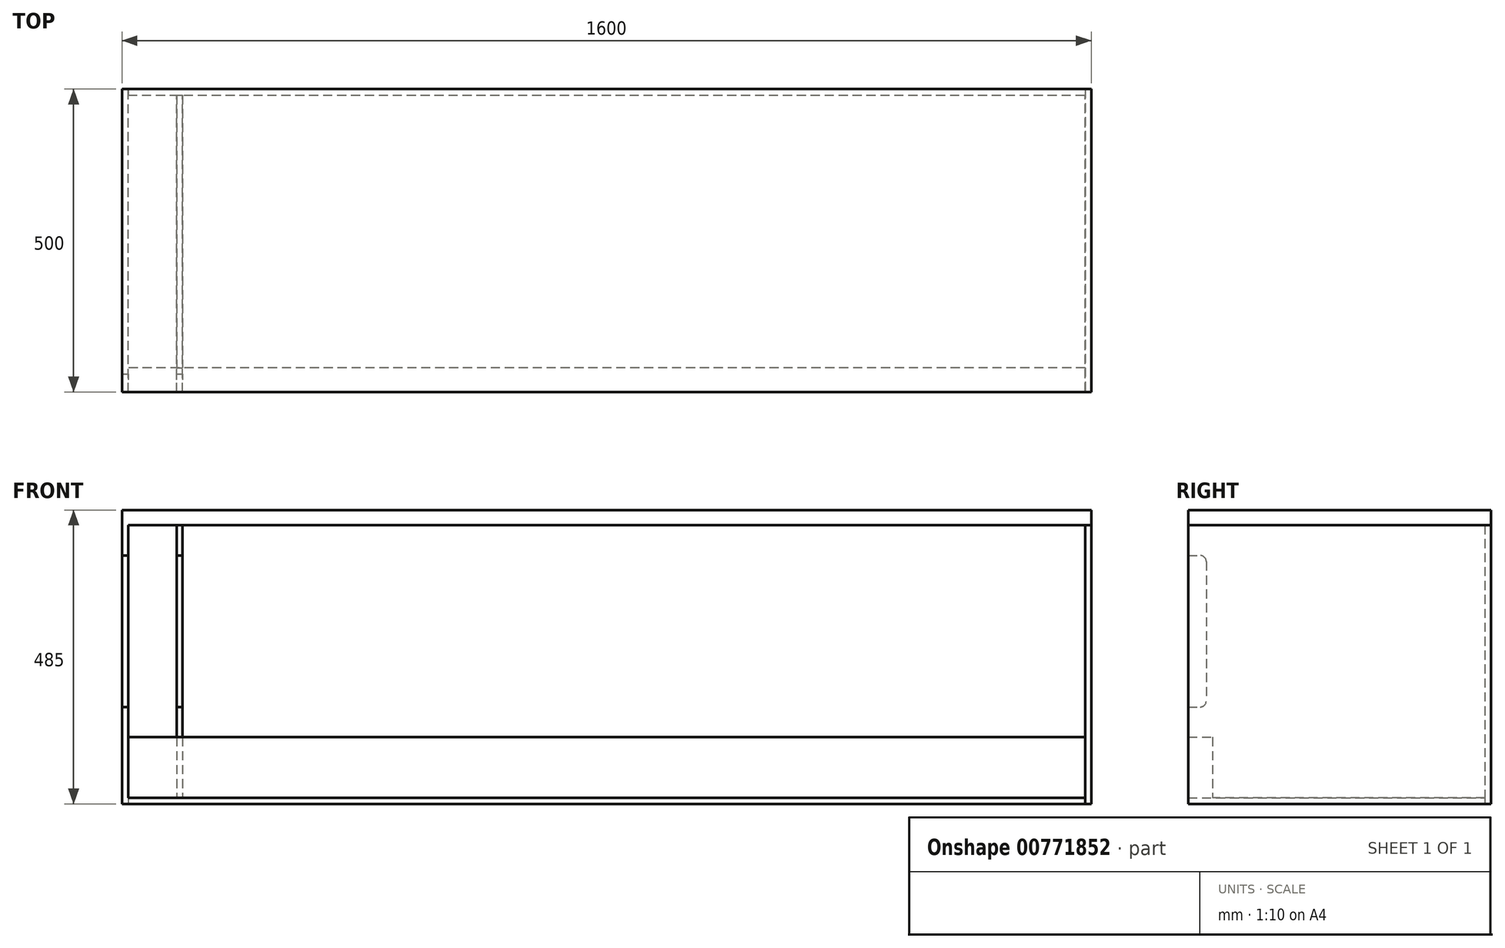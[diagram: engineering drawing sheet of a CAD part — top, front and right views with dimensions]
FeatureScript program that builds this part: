
annotation { "Feature Type Name" : "Feature", "Feature Type Description" : "" }
export const myFeature = defineFeature(function(context is Context, id is Id, definition is map)
    precondition{}
    {
        {
            var Q0;
            Q0=qCreatedBy(makeId("Top.planeOp"),FACE);
            var sketch = newSketch(context, id + "F0", { "sketchPlane" : qUnion([Q0])});
            skLineSegment(sketch, "E0.bottom", {"start": v(0, 0) * mm, "end": v(1600, 0) * mm});
            skLineSegment(sketch, "E0.top", {"start": v(0, 500) * mm, "end": v(1600, 500) * mm});
            skLineSegment(sketch, "E0.left", {"start": v(0, 0) * mm, "end": v(0, 500) * mm});
            skLineSegment(sketch, "E0.right", {"start": v(1600, 0) * mm, "end": v(1600, 500) * mm});
            skSolve(sketch);
        }
        {
            var Q0;
            Q0=makeQuery(id+"F0.imprint","IMPRINT",FACE,{"disambiguationData":[TD([[makeQuery(id+"F0.imprint","IMPRINT",EDGE,{"derivedFrom":sQuery(id+"F0.wireOp",EDGE,"E0.bottom")}),1.0]])]});
            extrude(context, id + "F1", {"entities" : qUnion([Q0]), "depth" : 25 * mm, "offsetDistance" : 25 * mm});
        }
        {
            var Q0;
            Q0=makeQuery(id+"F0.imprint","IMPRINT",FACE,{"disambiguationData":[TD([[makeQuery(id+"F0.imprint","IMPRINT",EDGE,{"derivedFrom":sQuery(id+"F0.wireOp",EDGE,"E0.bottom")}),1.0]])]});
            cPlane(context, id + "F2", {"entities" : qUnion([Q0]), "cplaneType" : CPlaneType.OFFSET, "offset" : 460 * mm, "oppositeDirection" : true, "width" : 150 * mm, "height" : 150 * mm});
        }
        {
            var Q0;
            Q0=qCreatedBy(id+"F2.planeOp",FACE);
            var sketch = newSketch(context, id + "F3", { "sketchPlane" : qUnion([Q0])});
            skLineSegment(sketch, "E1.bottom", {"start": v(10, 0) * mm, "end": v(1590, 0) * mm});
            skLineSegment(sketch, "E1.top", {"start": v(10, 490) * mm, "end": v(1590, 490) * mm});
            skLineSegment(sketch, "E1.left", {"start": v(10, 0) * mm, "end": v(10, 490) * mm});
            skLineSegment(sketch, "E1.right", {"start": v(1590, 0) * mm, "end": v(1590, 490) * mm});
            skSolve(sketch);
        }
        {
            var Q0;
            Q0=makeQuery(id+"F3.imprint","IMPRINT",FACE,{"disambiguationData":[TD([[makeQuery(id+"F3.imprint","IMPRINT",EDGE,{"derivedFrom":sQuery(id+"F3.wireOp",EDGE,"E1.bottom")}),1.0]])]});
            extrude(context, id + "F4", {"entities" : qUnion([Q0]), "depth" : 10 * mm, "offsetDistance" : 25 * mm});
        }
        {
            var Q0;
            Q0=makeQuery(id+"F0.imprint","IMPRINT",FACE,{"disambiguationData":[TD([[makeQuery(id+"F0.imprint","IMPRINT",EDGE,{"derivedFrom":sQuery(id+"F0.wireOp",EDGE,"E0.bottom")}),1.0]])]});
            var sketch = newSketch(context, id + "F5", { "sketchPlane" : qUnion([Q0])});
            skLineSegment(sketch, "E2.bottom", {"start": v(0, 0) * mm, "end": v(10, 0) * mm});
            skLineSegment(sketch, "E2.top", {"start": v(0, 500) * mm, "end": v(10, 500) * mm});
            skLineSegment(sketch, "E2.left", {"start": v(0, 0) * mm, "end": v(0, 500) * mm});
            skLineSegment(sketch, "E2.right", {"start": v(10, 0) * mm, "end": v(10, 500) * mm});
            skSolve(sketch);
        }
        {
            var Q0;
            Q0=qSketchRegion(id+"F5",true);
            var Q1;
            Q1=makeQuery(id+"F4.opExtrude","CAP_FACE",FACE,{"disambiguationData":[OSD([sQuery(id+"F3.wireOp",EDGE,"E1.bottom"),sQuery(id+"F3.wireOp",EDGE,"E1.top"),sQuery(id+"F3.wireOp",EDGE,"E1.left"),sQuery(id+"F3.wireOp",EDGE,"E1.right")])],"isStart":true});
            extrude(context, id + "F6", {"entities" : qUnion([Q0]), "operationType" : NewBodyOperationType.ADD, "endBound" : BoundingType.UP_TO_SURFACE, "oppositeDirection" : true, "depth" : 25 * mm, "endBoundEntityFace" : qUnion([Q1]), "offsetDistance" : 25 * mm});
        }
        {
            var Q0;
            Q0=makeQuery(id+"F0.imprint","IMPRINT",FACE,{"disambiguationData":[TD([[makeQuery(id+"F0.imprint","IMPRINT",EDGE,{"derivedFrom":sQuery(id+"F0.wireOp",EDGE,"E0.bottom")}),1.0]])]});
            var sketch = newSketch(context, id + "F7", { "sketchPlane" : qUnion([Q0])});
            skLineSegment(sketch, "E3.bottom", {"start": v(1600, 0) * mm, "end": v(1590, 0) * mm});
            skLineSegment(sketch, "E3.top", {"start": v(1600, 500) * mm, "end": v(1590, 500) * mm});
            skLineSegment(sketch, "E3.left", {"start": v(1600, 0) * mm, "end": v(1600, 500) * mm});
            skLineSegment(sketch, "E3.right", {"start": v(1590, 0) * mm, "end": v(1590, 500) * mm});
            skSolve(sketch);
        }
        {
            var Q0;
            Q0=makeQuery(id+"F7.imprint","IMPRINT",FACE,{"disambiguationData":[TD([[makeQuery(id+"F7.imprint","IMPRINT",EDGE,{"derivedFrom":sQuery(id+"F7.wireOp",EDGE,"E3.bottom")}),1.0]])]});
            var Q1;
            Q1=makeQuery(id+"F4.opExtrude","CAP_FACE",FACE,{"disambiguationData":[OSD([sQuery(id+"F3.wireOp",EDGE,"E1.bottom"),sQuery(id+"F3.wireOp",EDGE,"E1.top"),sQuery(id+"F3.wireOp",EDGE,"E1.left"),sQuery(id+"F3.wireOp",EDGE,"E1.right")])],"isStart":true});
            extrude(context, id + "F8", {"entities" : qUnion([Q0]), "endBound" : BoundingType.UP_TO_SURFACE, "oppositeDirection" : true, "depth" : 25 * mm, "endBoundEntityFace" : qUnion([Q1]), "offsetDistance" : 25 * mm});
        }
        {
            var Q0;
            Q0=makeQuery(id+"F6.opExtrude","SWEPT_FACE",FACE,{"disambiguationData":[OSD([sQuery(id+"F5.wireOp",EDGE,"E2.right")])]});
            var sketch = newSketch(context, id + "F9", { "sketchPlane" : qUnion([Q0])});
            skLineSegment(sketch, "E4.bottom", {"start": v(0, -350) * mm, "end": v(40, -350) * mm});
            skLineSegment(sketch, "E4.top", {"start": v(0, -450) * mm, "end": v(40, -450) * mm});
            skLineSegment(sketch, "E4.left", {"start": v(0, -350) * mm, "end": v(0, -450) * mm});
            skLineSegment(sketch, "E4.right", {"start": v(40, -350) * mm, "end": v(40, -450) * mm});
            skSolve(sketch);
        }
        {
            var Q0;
            Q0=makeQuery(id+"F9.imprint","IMPRINT",FACE,{"disambiguationData":[TD([[makeQuery(id+"F9.imprint","IMPRINT",EDGE,{"derivedFrom":sQuery(id+"F9.wireOp",EDGE,"E4.bottom")}),-1.0]])]});
            extrude(context, id + "F10", {"entities" : qUnion([Q0]), "endBound" : BoundingType.UP_TO_NEXT, "depth" : 25 * mm, "offsetDistance" : 25 * mm});
        }
        {
            var Q0;
            Q0=makeQuery(id+"F4.opExtrude","CAP_FACE",FACE,{"disambiguationData":[OSD([sQuery(id+"F3.wireOp",EDGE,"E1.bottom"),sQuery(id+"F3.wireOp",EDGE,"E1.top"),sQuery(id+"F3.wireOp",EDGE,"E1.left"),sQuery(id+"F3.wireOp",EDGE,"E1.right")])],"isStart":false});
            var sketch = newSketch(context, id + "F11", { "sketchPlane" : qUnion([Q0])});
            skLineSegment(sketch, "E5.bottom", {"start": v(100, 490) * mm, "end": v(90, 490) * mm});
            skLineSegment(sketch, "E5.top", {"start": v(100, 40) * mm, "end": v(90, 40) * mm});
            skLineSegment(sketch, "E5.left", {"start": v(100, 490) * mm, "end": v(100, 40) * mm});
            skLineSegment(sketch, "E5.right", {"start": v(90, 490) * mm, "end": v(90, 40) * mm});
            skSolve(sketch);
        }
        {
            var Q0;
            Q0=makeQuery(id+"F11.imprint","IMPRINT",FACE,{"disambiguationData":[TD([[makeQuery(id+"F11.imprint","IMPRINT",EDGE,{"derivedFrom":sQuery(id+"F11.wireOp",EDGE,"E5.bottom")}),-1.0]])]});
            extrude(context, id + "F12", {"entities" : qUnion([Q0]), "endBound" : BoundingType.UP_TO_NEXT, "depth" : 25 * mm, "offsetDistance" : 25 * mm});
        }
        {
            var Q0;
            Q0=makeQuery(id+"F12.opExtrude","SWEPT_FACE",FACE,{"disambiguationData":[OSD([sQuery(id+"F11.wireOp",EDGE,"E5.top")])]});
            var sketch = newSketch(context, id + "F13", { "sketchPlane" : qUnion([Q0])});
            skLineSegment(sketch, "E6.bottom", {"start": v(90, 0) * mm, "end": v(100, 0) * mm});
            skLineSegment(sketch, "E6.top", {"start": v(90, -350) * mm, "end": v(100, -350) * mm});
            skLineSegment(sketch, "E6.left", {"start": v(90, 0) * mm, "end": v(90, -350) * mm});
            skLineSegment(sketch, "E6.right", {"start": v(100, 0) * mm, "end": v(100, -350) * mm});
            skSolve(sketch);
        }
        {
            var Q0;
            Q0=makeQuery(id+"F13.imprint","IMPRINT",FACE,{"disambiguationData":[TD([[makeQuery(id+"F13.imprint","IMPRINT",EDGE,{"derivedFrom":sQuery(id+"F13.wireOp",EDGE,"E6.bottom")}),1.0]])]});
            var Q1;
            Q1=makeQuery(id+"F10.opExtrude","SWEPT_FACE",FACE,{"disambiguationData":[OSD([sQuery(id+"F9.wireOp",EDGE,"E4.left")])]});
            extrude(context, id + "F14", {"entities" : qUnion([Q0]), "endBound" : BoundingType.UP_TO_SURFACE, "depth" : 25 * mm, "endBoundEntityFace" : qUnion([Q1]), "offsetDistance" : 25 * mm});
        }
        {
            var Q0;
            Q0=makeQuery(id+"F14.opExtrude","SWEPT_BODY",BODY,{"disambiguationData":[OSD([sQuery(id+"F13.wireOp",EDGE,"E6.bottom"),sQuery(id+"F13.wireOp",EDGE,"E6.top"),sQuery(id+"F13.wireOp",EDGE,"E6.left"),sQuery(id+"F13.wireOp",EDGE,"E6.right")])]});
            var Q1;
            Q1=makeQuery(id+"F12.opExtrude","SWEPT_BODY",BODY,{"disambiguationData":[OSD([sQuery(id+"F11.wireOp",EDGE,"E5.bottom"),sQuery(id+"F11.wireOp",EDGE,"E5.top"),sQuery(id+"F11.wireOp",EDGE,"E5.left"),sQuery(id+"F11.wireOp",EDGE,"E5.right")])]});
            booleanBodies(context, id + "F15", {"operationType" : BooleanOperationType.UNION, "tools" : qUnion([Q0, Q1])});
        }
        {
            var Q0;
            Q0=makeQuery(id+"F15.opBoolean","MERGE",FACE,{"derivedFrom":[makeQuery(id+"F12.opExtrude","SWEPT_FACE",FACE,{"disambiguationData":[OSD([sQuery(id+"F11.wireOp",EDGE,"E5.left")])]}),makeQuery(id+"F14.opExtrude","SWEPT_FACE",FACE,{"disambiguationData":[OSD([sQuery(id+"F13.wireOp",EDGE,"E6.right")])]})]});
            var sketch = newSketch(context, id + "F16", { "sketchPlane" : qUnion([Q0])});
            skLineSegment(sketch, "E7.bottom", {"start": v(0, -50) * mm, "end": v(30, -50) * mm});
            skLineSegment(sketch, "E7.top", {"start": v(0, -300) * mm, "end": v(30, -300) * mm});
            skLineSegment(sketch, "E7.left", {"start": v(0, -50) * mm, "end": v(0, -300) * mm});
            skLineSegment(sketch, "E7.right", {"start": v(30, -50) * mm, "end": v(30, -300) * mm});
            skSolve(sketch);
        }
        {
            var Q0;
            Q0=makeQuery(id+"F16.imprint","IMPRINT",FACE,{"disambiguationData":[TD([[makeQuery(id+"F16.imprint","IMPRINT",EDGE,{"derivedFrom":sQuery(id+"F16.wireOp",EDGE,"E7.bottom")}),-1.0]])]});
            extrude(context, id + "F17", {"entities" : qUnion([Q0]), "operationType" : NewBodyOperationType.REMOVE, "endBound" : BoundingType.THROUGH_ALL, "oppositeDirection" : true, "depth" : 25 * mm, "offsetDistance" : 25 * mm});
        }
        {
            var Q0;
            Q0=makeQuery(id+"F17.boolean.opBoolean","COPY",EDGE,{"derivedFrom":makeQuery(id+"F17.opExtrude","SWEPT_EDGE",EDGE,{"disambiguationData":[OSD([sQuery(id+"F16.wireOp",EDGE,"E7.bottom"),sQuery(id+"F16.wireOp",EDGE,"E7.right")])]})});
            var Q1;
            Q1=makeQuery(id+"F17.boolean.opBoolean","COPY",EDGE,{"derivedFrom":makeQuery(id+"F17.opExtrude","SWEPT_EDGE",EDGE,{"disambiguationData":[OSD([sQuery(id+"F16.wireOp",EDGE,"E7.top"),sQuery(id+"F16.wireOp",EDGE,"E7.right")])]})});
            fillet(context, id + "F18", {"entities" : qUnion([Q0, Q1]), "radius" : 10 * mm, "tangentPropagation" : true, "allowEdgeOverflow" : false});
        }
    });
